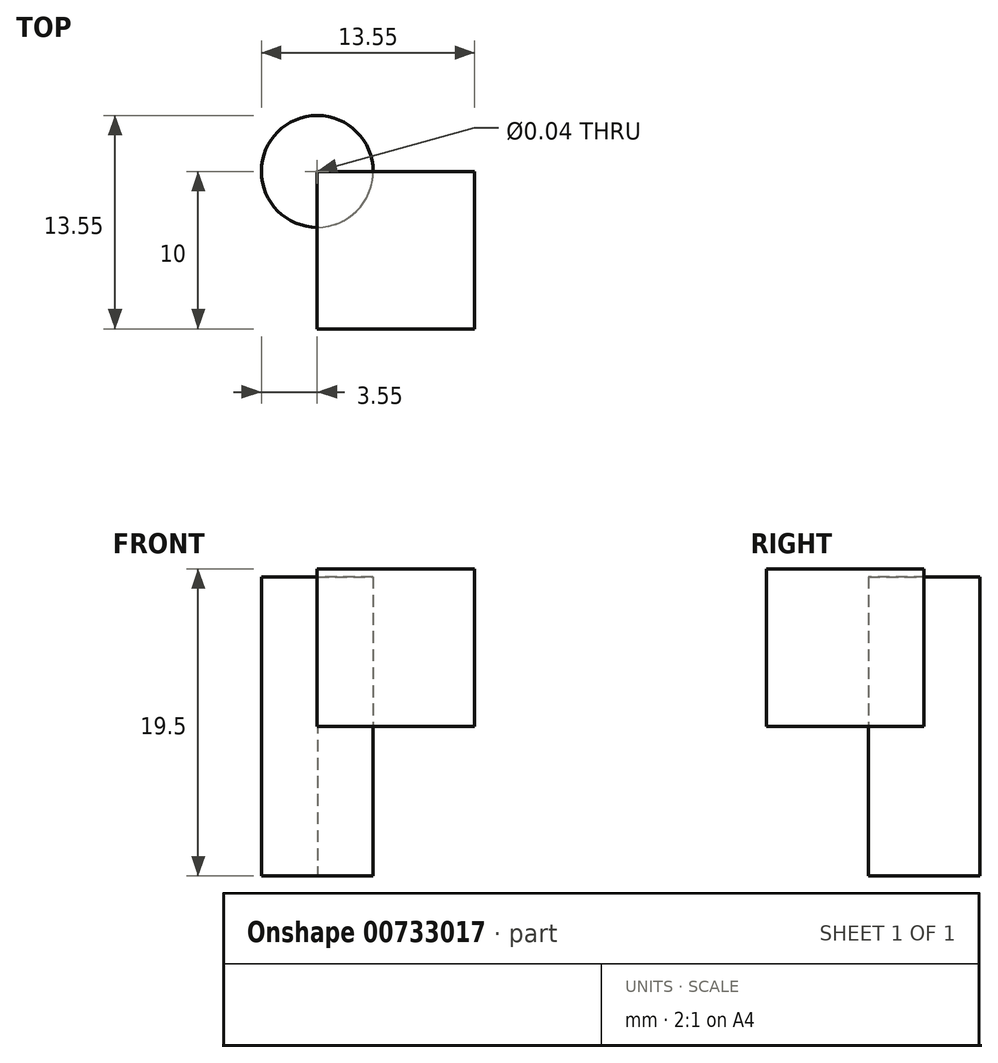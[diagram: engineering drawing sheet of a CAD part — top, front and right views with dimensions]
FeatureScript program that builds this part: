
annotation { "Feature Type Name" : "Feature", "Feature Type Description" : "" }
export const myFeature = defineFeature(function(context is Context, id is Id, definition is map)
    precondition{}
    {
        {
            var Q0;
            Q0=qCreatedBy(makeId("Top.planeOp"),FACE);
            var sketch = newSketch(context, id + "F0", { "sketchPlane" : qUnion([Q0])});
            skCircle(sketch, "E0", {"center": v(0, 0) * mm, "radius": 0.02 * mm});
            skCircle(sketch, "E1", {"center": v(0, 0) * mm, "radius": 3.55 * mm});
            skSolve(sketch);
        }
        {
            var Q0;
            Q0=makeQuery(id+"F0.imprint","IMPRINT",FACE,{"disambiguationData":[TD([[makeQuery(id+"F0.imprint","IMPRINT",EDGE,{"derivedFrom":sQuery(id+"F0.wireOp",EDGE,"E0")}),-1.0]])]});
            extrude(context, id + "F1", {"entities" : qUnion([Q0]), "endBound" : BoundingType.SYMMETRIC, "depth" : 19 * mm, "offsetDistance" : 25 * mm});
        }
        {
            var Q0;
            Q0=qCreatedBy(makeId("Front.planeOp"),FACE);
            var sketch = newSketch(context, id + "F2", { "sketchPlane" : qUnion([Q0])});
            skLineSegment(sketch, "E2.bottom", {"start": v(0, 0) * mm, "end": v(10, 0) * mm});
            skLineSegment(sketch, "E2.top", {"start": v(0, 10) * mm, "end": v(10, 10) * mm});
            skLineSegment(sketch, "E2.left", {"start": v(0, 0) * mm, "end": v(0, 10) * mm});
            skLineSegment(sketch, "E2.right", {"start": v(10, 0) * mm, "end": v(10, 10) * mm});
            skSolve(sketch);
        }
        {
            var Q0;
            Q0=makeQuery(id+"F2.imprint","IMPRINT",FACE,{"disambiguationData":[TD([[makeQuery(id+"F2.imprint","IMPRINT",EDGE,{"derivedFrom":sQuery(id+"F2.wireOp",EDGE,"E2.bottom")}),1.0]])]});
            extrude(context, id + "F3", {"entities" : qUnion([Q0]), "depth" : 10 * mm, "offsetDistance" : 25 * mm});
        }
    });
